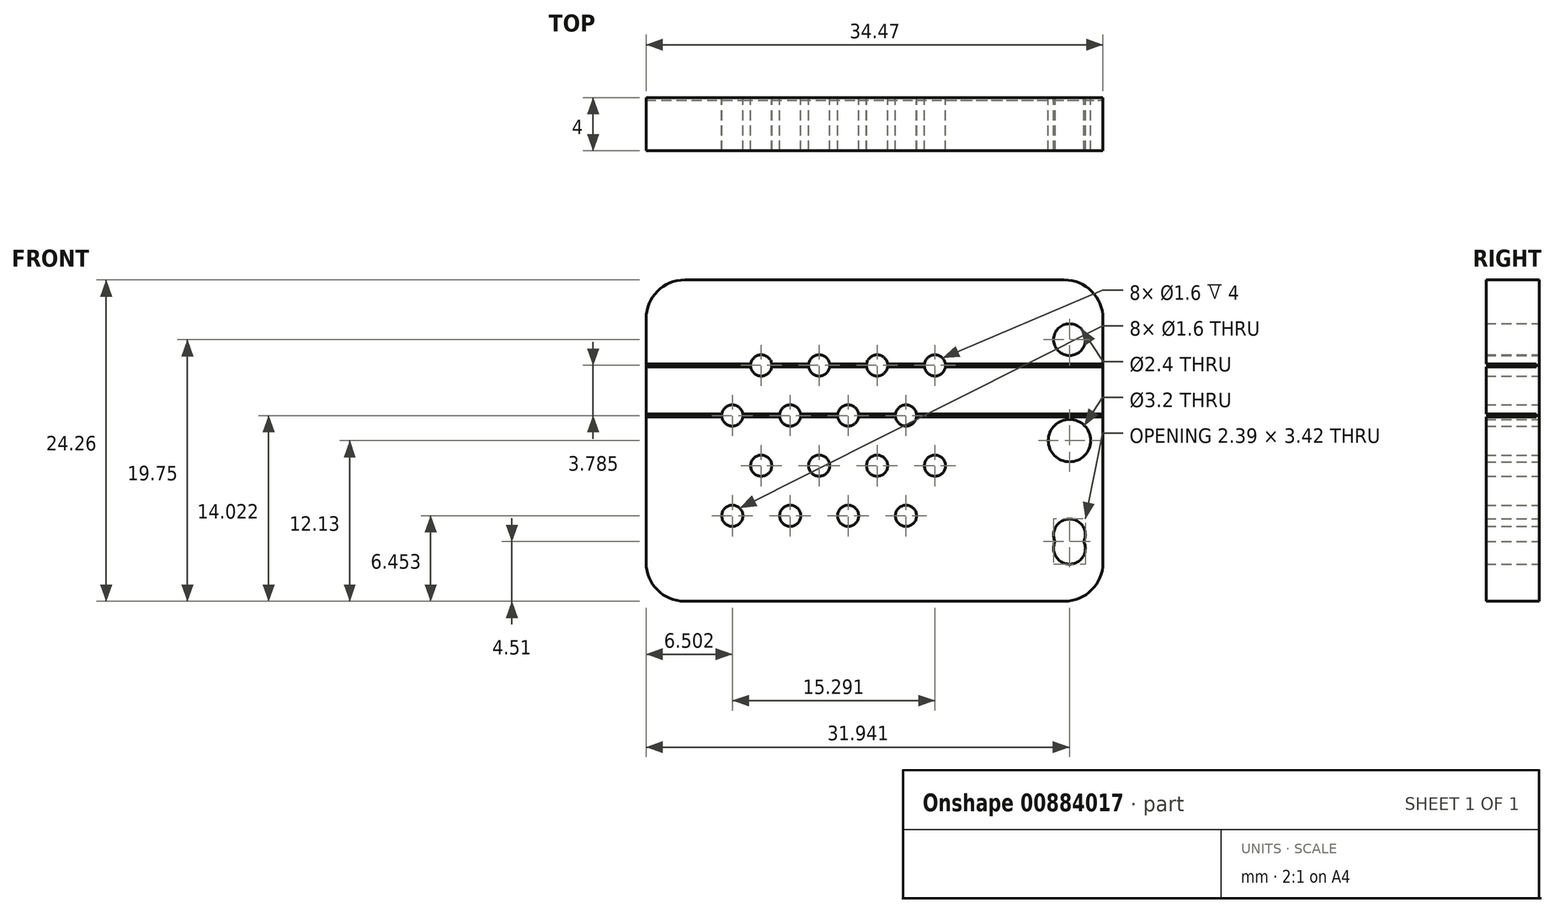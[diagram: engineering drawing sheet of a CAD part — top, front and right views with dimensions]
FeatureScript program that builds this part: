
annotation { "Feature Type Name" : "Feature", "Feature Type Description" : "" }
export const myFeature = defineFeature(function(context is Context, id is Id, definition is map)
    precondition{}
    {
        {
            var Q0;
            Q0=qCreatedBy(makeId("Front.planeOp"),FACE);
            var sketch = newSketch(context, id + "F0", { "sketchPlane" : qUnion([Q0])});
            skArc(sketch, "E0", {"start": v(-105.6, -27.46) * mm, "mid": v(-107.66, -28.32) * mm, "end": v(-108.52, -30.38) * mm});
            skArc(sketch, "E1", {"start": v(-108.52, -48.8) * mm, "mid": v(-107.66, -50.86) * mm, "end": v(-105.6, -51.72) * mm});
            skArc(sketch, "E2", {"start": v(-76.97, -51.72) * mm, "mid": v(-74.9, -50.86) * mm, "end": v(-74.05, -48.8) * mm});
            skArc(sketch, "E3", {"start": v(-74.05, -30.38) * mm, "mid": v(-74.9, -28.32) * mm, "end": v(-76.97, -27.46) * mm});
            skLineSegment(sketch, "E4", {"start": v(-105.6, -27.46) * mm, "end": v(-76.97, -27.46) * mm});
            skLineSegment(sketch, "E5", {"start": v(-74.05, -30.38) * mm, "end": v(-74.05, -48.8) * mm});
            skLineSegment(sketch, "E6", {"start": v(-76.97, -51.72) * mm, "end": v(-105.6, -51.72) * mm});
            skLineSegment(sketch, "E7", {"start": v(-108.52, -48.8) * mm, "end": v(-108.52, -30.38) * mm});
            skCircle(sketch, "E8", {"center": v(-99.83, -33.91) * mm, "radius": 0.8 * mm});
            skCircle(sketch, "E9", {"center": v(-95.46, -33.91) * mm, "radius": 0.8 * mm});
            skCircle(sketch, "E10", {"center": v(-91.1, -33.91) * mm, "radius": 0.8 * mm});
            skCircle(sketch, "E11", {"center": v(-86.73, -33.91) * mm, "radius": 0.8 * mm});
            skCircle(sketch, "E12", {"center": v(-102.02, -37.7) * mm, "radius": 0.8 * mm});
            skCircle(sketch, "E13", {"center": v(-97.65, -37.7) * mm, "radius": 0.8 * mm});
            skCircle(sketch, "E14", {"center": v(-93.28, -37.7) * mm, "radius": 0.8 * mm});
            skCircle(sketch, "E15", {"center": v(-88.91, -37.7) * mm, "radius": 0.8 * mm});
            skCircle(sketch, "E16", {"center": v(-99.83, -41.48) * mm, "radius": 0.8 * mm});
            skCircle(sketch, "E17", {"center": v(-95.46, -41.48) * mm, "radius": 0.8 * mm});
            skCircle(sketch, "E18", {"center": v(-91.1, -41.48) * mm, "radius": 0.8 * mm});
            skCircle(sketch, "E19", {"center": v(-86.73, -41.48) * mm, "radius": 0.8 * mm});
            skCircle(sketch, "E20", {"center": v(-102.02, -45.27) * mm, "radius": 0.8 * mm});
            skCircle(sketch, "E21", {"center": v(-97.65, -45.27) * mm, "radius": 0.8 * mm});
            skCircle(sketch, "E22", {"center": v(-93.28, -45.27) * mm, "radius": 0.8 * mm});
            skCircle(sketch, "E23", {"center": v(-88.91, -45.27) * mm, "radius": 0.8 * mm});
            skCircle(sketch, "E24", {"center": v(-76.58, -39.6) * mm, "radius": 1.6 * mm});
            skCircle(sketch, "E25", {"center": v(-76.58, -31.97) * mm, "radius": 1.2 * mm});
            skCircle(sketch, "E26", {"center": v(-76.58, -46.7) * mm, "radius": 1.2 * mm});
            skCircle(sketch, "E27", {"center": v(-76.58, -47.72) * mm, "radius": 1.2 * mm});
            skSolve(sketch);
        }
        {
            var Q0;
            Q0=makeQuery(id+"F0.imprint","IMPRINT",FACE,{"disambiguationData":[TD([[makeQuery(id+"F0.imprint","IMPRINT",EDGE,{"derivedFrom":sQuery(id+"F0.wireOp",EDGE,"E0")}),1.0]])]});
            extrude(context, id + "F1", {"entities" : qUnion([Q0]), "depth" : 4 * mm, "offsetDistance" : 25 * mm});
        }
        {
            var Q0;
            Q0=makeQuery(id+"F1.opExtrude","CAP_FACE",FACE,{"disambiguationData":[OSD([sQuery(id+"F0.wireOp",EDGE,"E0"),sQuery(id+"F0.wireOp",EDGE,"E1"),sQuery(id+"F0.wireOp",EDGE,"E2"),sQuery(id+"F0.wireOp",EDGE,"E3"),sQuery(id+"F0.wireOp",EDGE,"E4"),sQuery(id+"F0.wireOp",EDGE,"E5"),sQuery(id+"F0.wireOp",EDGE,"E6"),sQuery(id+"F0.wireOp",EDGE,"E7"),sQuery(id+"F0.wireOp",EDGE,"E8"),sQuery(id+"F0.wireOp",EDGE,"E9"),sQuery(id+"F0.wireOp",EDGE,"E10"),sQuery(id+"F0.wireOp",EDGE,"E11"),sQuery(id+"F0.wireOp",EDGE,"E12"),sQuery(id+"F0.wireOp",EDGE,"E13"),sQuery(id+"F0.wireOp",EDGE,"E14"),sQuery(id+"F0.wireOp",EDGE,"E15"),sQuery(id+"F0.wireOp",EDGE,"E16"),sQuery(id+"F0.wireOp",EDGE,"E17"),sQuery(id+"F0.wireOp",EDGE,"E18"),sQuery(id+"F0.wireOp",EDGE,"E19"),sQuery(id+"F0.wireOp",EDGE,"E20"),sQuery(id+"F0.wireOp",EDGE,"E21"),sQuery(id+"F0.wireOp",EDGE,"E22"),sQuery(id+"F0.wireOp",EDGE,"E23"),sQuery(id+"F0.wireOp",EDGE,"E24"),sQuery(id+"F0.wireOp",EDGE,"E25"),sQuery(id+"F0.wireOp",EDGE,"E26"),sQuery(id+"F0.wireOp",EDGE,"E27")])],"isStart":false});
            var sketch = newSketch(context, id + "F2", { "sketchPlane" : qUnion([Q0])});
            skLineSegment(sketch, "E28", {"start": v(-99.83, -33.91) * mm, "end": v(-86.73, -33.91) * mm, "construction": true});
            skLineSegment(sketch, "E29", {"start": v(-102.02, -37.7) * mm, "end": v(-88.91, -37.7) * mm, "construction": true});
            skLineSegment(sketch, "E30.bottom", {"start": v(-108.52, -33.81) * mm, "end": v(-74.05, -33.81) * mm});
            skLineSegment(sketch, "E30.top", {"start": v(-108.52, -34.01) * mm, "end": v(-74.05, -34.01) * mm});
            skLineSegment(sketch, "E30.left", {"start": v(-108.52, -33.81) * mm, "end": v(-108.52, -34.01) * mm});
            skLineSegment(sketch, "E30.right", {"start": v(-74.05, -33.81) * mm, "end": v(-74.05, -34.01) * mm});
            skLineSegment(sketch, "E31.bottom", {"start": v(-108.52, -37.6) * mm, "end": v(-74.05, -37.6) * mm});
            skLineSegment(sketch, "E31.top", {"start": v(-108.52, -37.8) * mm, "end": v(-74.05, -37.8) * mm});
            skLineSegment(sketch, "E31.left", {"start": v(-108.52, -37.6) * mm, "end": v(-108.52, -37.8) * mm});
            skLineSegment(sketch, "E31.right", {"start": v(-74.05, -37.6) * mm, "end": v(-74.05, -37.8) * mm});
            skSolve(sketch);
        }
        {
            var Q0;
            Q0 = qSketchRegion(id + "F2", true);
            extrude(context, id + "F3", {"entities" : qUnion([Q0]), "operationType" : NewBodyOperationType.REMOVE, "oppositeDirection" : true, "depth" : 3.8 * mm, "offsetDistance" : 25 * mm});
        }
    });
